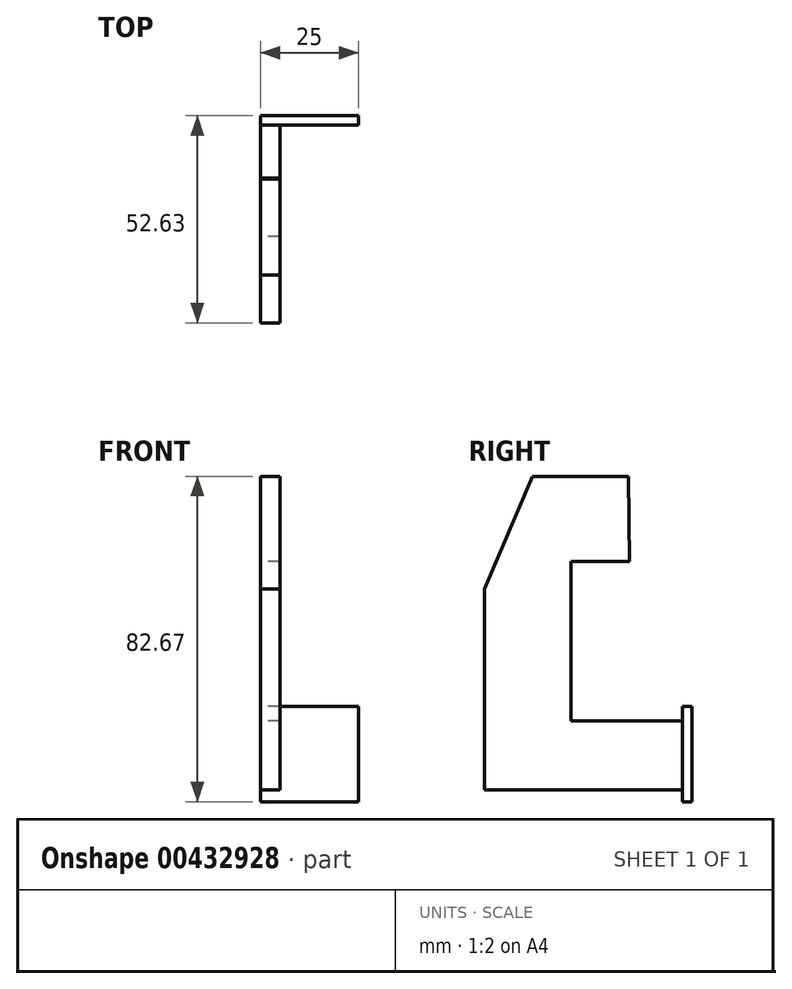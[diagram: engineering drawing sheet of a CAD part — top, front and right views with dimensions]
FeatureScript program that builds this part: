
annotation { "Feature Type Name" : "Feature", "Feature Type Description" : "" }
export const myFeature = defineFeature(function(context is Context, id is Id, definition is map)
    precondition{}
    {
        {
            var Q0;
            Q0=qCreatedBy(makeId("Right.planeOp"),FACE);
            var sketch = newSketch(context, id + "F0", { "sketchPlane" : qUnion([Q0])});
            skLineSegment(sketch, "E0", {"start": v(14.65, 21.65) * mm, "end": v(-9.76, 21.65) * mm});
            skLineSegment(sketch, "E1", {"start": v(-9.76, 21.65) * mm, "end": v(-21.93, -6.9) * mm});
            skLineSegment(sketch, "E2", {"start": v(-21.93, -6.9) * mm, "end": v(-21.93, -58.04) * mm});
            skLineSegment(sketch, "E3", {"start": v(-21.93, -58.04) * mm, "end": v(28.27, -58.04) * mm});
            skLineSegment(sketch, "E4", {"start": v(28.27, -58.04) * mm, "end": v(28.27, -40.5) * mm});
            skLineSegment(sketch, "E5", {"start": v(28.27, -40.5) * mm, "end": v(0, -40.5) * mm});
            skLineSegment(sketch, "E6", {"start": v(0, -40.5) * mm, "end": v(0, 0) * mm});
            skLineSegment(sketch, "E7", {"start": v(0, 0) * mm, "end": v(14.84, 0) * mm});
            skLineSegment(sketch, "E8", {"start": v(14.84, 0) * mm, "end": v(14.65, 21.65) * mm});
            skSolve(sketch);
        }
        {
            var Q0;
            Q0=makeQuery(id+"F0.imprint","IMPRINT",FACE,{"disambiguationData":[TD([[makeQuery(id+"F0.imprint","IMPRINT",EDGE,{"derivedFrom":sQuery(id+"F0.wireOp",EDGE,"E0")}),1.0]])]});
            extrude(context, id + "F1", {"entities" : qUnion([Q0]), "depth" : 5 * mm});
        }
        {
            var Q0;
            Q0=qCreatedBy(makeId("Right.planeOp"),FACE);
            var sketch = newSketch(context, id + "F2", { "sketchPlane" : qUnion([Q0])});
            skLineSegment(sketch, "E9.bottom", {"start": v(30.7, -36.76) * mm, "end": v(28.27, -36.76) * mm});
            skLineSegment(sketch, "E9.top", {"start": v(30.7, -61.02) * mm, "end": v(28.27, -61.02) * mm});
            skLineSegment(sketch, "E9.left", {"start": v(30.7, -36.76) * mm, "end": v(30.7, -61.02) * mm});
            skLineSegment(sketch, "E9.right", {"start": v(28.27, -36.76) * mm, "end": v(28.27, -61.02) * mm});
            skSolve(sketch);
        }
        {
            var Q0;
            Q0=makeQuery(id+"F2.imprint","IMPRINT",FACE,{"disambiguationData":[TD([[makeQuery(id+"F2.imprint","IMPRINT",EDGE,{"derivedFrom":sQuery(id+"F2.wireOp",EDGE,"E9.bottom")}),1.0]])]});
            extrude(context, id + "F3", {"entities" : qUnion([Q0]), "operationType" : NewBodyOperationType.ADD, "depth" : 25 * mm});
        }
    });
